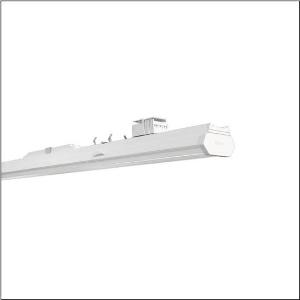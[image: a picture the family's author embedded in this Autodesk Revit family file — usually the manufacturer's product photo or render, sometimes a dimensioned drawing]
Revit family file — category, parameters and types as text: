
# Revit family: licross_r__21_protected_mo_52td12dn48xg_f2a3
name_source: partatom
category: Lighting Fixtures
units: mm (PartAtom-declared; Revit-internal decimal feet)

## family parameters
Cut with Voids When Loaded = No
Host = Face
Light Source = No
Part Type = Normal
Room Calculation Point = No
Round Connector Dimension = Use Diameter
Shared = No

## types (1)
- --- (1 x LED, 8000 lm, 45.3 W, 4000K)
    Apparent Load = 45 VA
    CIE Flux Codes = 73 92 98 99 100
    Color Rendering = 80
    Color Temperature = 4000K
    Default Elevation = 1800 mm
    Description = Licross® 21 Protected MO, luminaire insert, of sheet steel, galvanised, coil coated, white, length: 1.500mm, width: 90mm, height: 103mm, LED rated luminous flux: 8.000lm, light colour: 840, control gear: DALI 2, with plug, 5-pole, with phase selection, mains connection: 220..240V, AC, 50/60Hz, rated input power: 45W, halogen-free wiring, primary light control with lens, of plastic, primary optical cover: cover, of PMMA, light emission: direct distribution, primary light characteristic: symmetric, protection rating (complete): IP54, insulation class (complete): insulation class I (protective earthing), certification: CE, ENEC, VDE, UKCA, protection symbol: D if used in an environment with non-conductive dust loads with corresponding accessories, impact resistance: IK06, permissible ambient temperature for indoor applications: -25..+45°C, corresponds to IFS (International Featured Standards) requirements for safety and quality in the food industry, reducing of maximum allowable ambient temperature of 5°C with ceiling mounting, LABS conformity tested according to VDMA 24364:2018-05, packaging unit: 1 piece
    Height = 92 mm
    Lamp = 1 x LED
    Lamp Light Flux = 8000 lm
    Lamp Power = 45.3 W
    Lamp count = 1
    Length = 1500 mm
    Luminous efficacy = 177 lm/W
    Manufacturer = Siteco
    ModVariant = No
    Model = 52TD12DN48XG
    Mounting Place = Ceiling
    Mounting Type = Pendant
    Number of Poles = 1
    OnlyDefault = Yes
    Power Factor = 1
    Product Name = Licross® 21 Protected MO
    Product group = luminaire insert
    ProductGroupID = 901
    Protection Class = Protection class I
    Protection Degree = IP 54
    RLX_Detail_Level = 1
    RLX_Emergency_Light_Flux = 0 lm
    RLX_Emergency_Type = 0
    RLX_Emergency_Type_DB = No
    RlxData = <blob elided: 24405 chars, md5=39b91a27>
    Socket = socket
    Standby Power = 0 W
    System Light Flux = 8000 lm
    System Power = 45 W
    Type Comments = factory setting: luminous flux: 100 % | dim-lin: 254 | 305 mA
    Type Image = l_1256148.jpg
    URL = http://relux.com
    VarID = @adj_060331
    Voltage = 0 V
    Weight = 0.00 kg
    Width = 88 mm

## geometry (parser evidence)
native form markers: Blend x4, Sweep x9
no freeform markers — native parametric forms only
